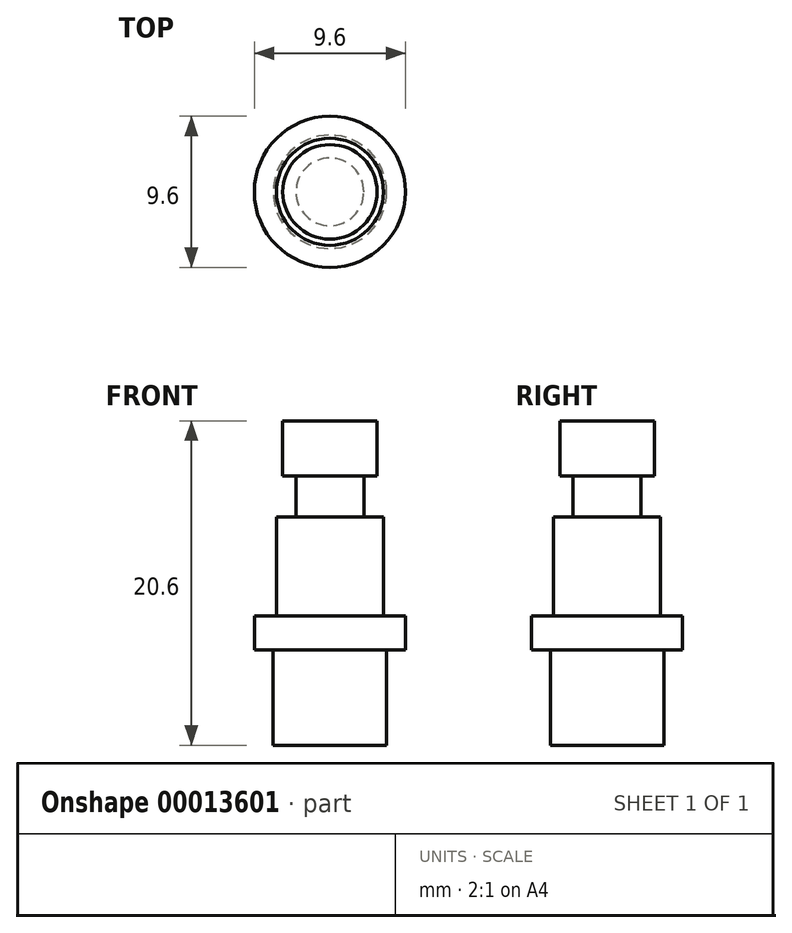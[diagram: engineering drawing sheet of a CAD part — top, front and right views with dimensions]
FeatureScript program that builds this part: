
annotation { "Feature Type Name" : "Feature", "Feature Type Description" : "" }
export const myFeature = defineFeature(function(context is Context, id is Id, definition is map)
    precondition{}
    {
        {
            var Q0;
            Q0=qCreatedBy(makeId("Top.planeOp"),FACE);
            var sketch = newSketch(context, id + "F0", { "sketchPlane" : qUnion([Q0])});
            skCircle(sketch, "E0", {"center": v(0, 0) * mm, "radius": 4.8 * mm});
            skCircle(sketch, "E1", {"center": v(0, 0) * mm, "radius": 3.4 * mm});
            skCircle(sketch, "E2", {"center": v(0, 0) * mm, "radius": 3.6 * mm});
            skCircle(sketch, "E3", {"center": v(0, 0) * mm, "radius": 2.15 * mm});
            skCircle(sketch, "E4", {"center": v(0, 0) * mm, "radius": 3 * mm});
            skSolve(sketch);
        }
        {
            var Q0;
            Q0=makeQuery(id+"F0.imprint","IMPRINT",FACE,{"disambiguationData":[TD([[makeQuery(id+"F0.imprint","IMPRINT",EDGE,{"derivedFrom":sQuery(id+"F0.wireOp",EDGE,"E1")}),-1.0]])]});
            var Q1;
            Q1=makeQuery(id+"F0.imprint","IMPRINT",FACE,{"disambiguationData":[TD([[makeQuery(id+"F0.imprint","IMPRINT",EDGE,{"derivedFrom":sQuery(id+"F0.wireOp",EDGE,"E1")}),1.0]])]});
            var Q2;
            Q2=makeQuery(id+"F0.imprint","IMPRINT",FACE,{"disambiguationData":[TD([[makeQuery(id+"F0.imprint","IMPRINT",EDGE,{"derivedFrom":sQuery(id+"F0.wireOp",EDGE,"E3")}),-1.0]])]});
            var Q3;
            Q3=makeQuery(id+"F0.imprint","IMPRINT",FACE,{"disambiguationData":[TD([[makeQuery(id+"F0.imprint","IMPRINT",EDGE,{"derivedFrom":sQuery(id+"F0.wireOp",EDGE,"E3")}),1.0]])]});
            extrude(context, id + "F1", {"entities" : qUnion([Q0, Q1, Q2, Q3]), "oppositeDirection" : true, "depth" : 8.2 * mm});
        }
        {
            var Q0;
            Q0=makeQuery(id+"F0.imprint","IMPRINT",FACE,{"disambiguationData":[TD([[makeQuery(id+"F0.imprint","IMPRINT",EDGE,{"derivedFrom":sQuery(id+"F0.wireOp",EDGE,"E3")}),1.0]])]});
            var Q1;
            Q1=makeQuery(id+"F0.imprint","IMPRINT",FACE,{"disambiguationData":[TD([[makeQuery(id+"F0.imprint","IMPRINT",EDGE,{"derivedFrom":sQuery(id+"F0.wireOp",EDGE,"E3")}),-1.0]])]});
            var Q2;
            Q2=makeQuery(id+"F0.imprint","IMPRINT",FACE,{"disambiguationData":[TD([[makeQuery(id+"F0.imprint","IMPRINT",EDGE,{"derivedFrom":sQuery(id+"F0.wireOp",EDGE,"E1")}),1.0]])]});
            var Q3;
            Q3=makeQuery(id+"F0.imprint","IMPRINT",FACE,{"disambiguationData":[TD([[makeQuery(id+"F0.imprint","IMPRINT",EDGE,{"derivedFrom":sQuery(id+"F0.wireOp",EDGE,"E1")}),-1.0]])]});
            var Q4;
            Q4=makeQuery(id+"F0.imprint","IMPRINT",FACE,{"disambiguationData":[TD([[makeQuery(id+"F0.imprint","IMPRINT",EDGE,{"derivedFrom":sQuery(id+"F0.wireOp",EDGE,"E0")}),1.0]])]});
            extrude(context, id + "F2", {"entities" : qUnion([Q0, Q1, Q2, Q3, Q4]), "operationType" : NewBodyOperationType.ADD, "oppositeDirection" : true, "depth" : 2.15 * mm});
        }
        {
            var Q0;
            Q0=makeQuery(id+"F0.imprint","IMPRINT",FACE,{"disambiguationData":[TD([[makeQuery(id+"F0.imprint","IMPRINT",EDGE,{"derivedFrom":sQuery(id+"F0.wireOp",EDGE,"E3")}),1.0]])]});
            extrude(context, id + "F3", {"entities" : qUnion([Q0]), "operationType" : NewBodyOperationType.ADD, "depth" : 12.4 * mm});
        }
        {
            var Q0;
            Q0=makeQuery(id+"F0.imprint","IMPRINT",FACE,{"disambiguationData":[TD([[makeQuery(id+"F0.imprint","IMPRINT",EDGE,{"derivedFrom":sQuery(id+"F0.wireOp",EDGE,"E3")}),-1.0]])]});
            extrude(context, id + "F4", {"entities" : qUnion([Q0]), "operationType" : NewBodyOperationType.ADD, "depth" : 12.4 * mm});
        }
        {
            var Q0;
            Q0=makeQuery(id+"F0.imprint","IMPRINT",FACE,{"disambiguationData":[TD([[makeQuery(id+"F0.imprint","IMPRINT",EDGE,{"derivedFrom":sQuery(id+"F0.wireOp",EDGE,"E3")}),-1.0]])]});
            extrude(context, id + "F5", {"entities" : qUnion([Q0]), "operationType" : NewBodyOperationType.REMOVE, "depth" : (12.4 - 3.5) * mm});
        }
        {
            var Q0;
            Q0=makeQuery(id+"F0.imprint","IMPRINT",FACE,{"disambiguationData":[TD([[makeQuery(id+"F0.imprint","IMPRINT",EDGE,{"derivedFrom":sQuery(id+"F0.wireOp",EDGE,"E3")}),-1.0]])]});
            var Q1;
            Q1=makeQuery(id+"F0.imprint","IMPRINT",FACE,{"disambiguationData":[TD([[makeQuery(id+"F0.imprint","IMPRINT",EDGE,{"derivedFrom":sQuery(id+"F0.wireOp",EDGE,"E1")}),1.0]])]});
            extrude(context, id + "F6", {"entities" : qUnion([Q0, Q1]), "operationType" : NewBodyOperationType.ADD, "depth" : 6.3 * mm});
        }
    });
